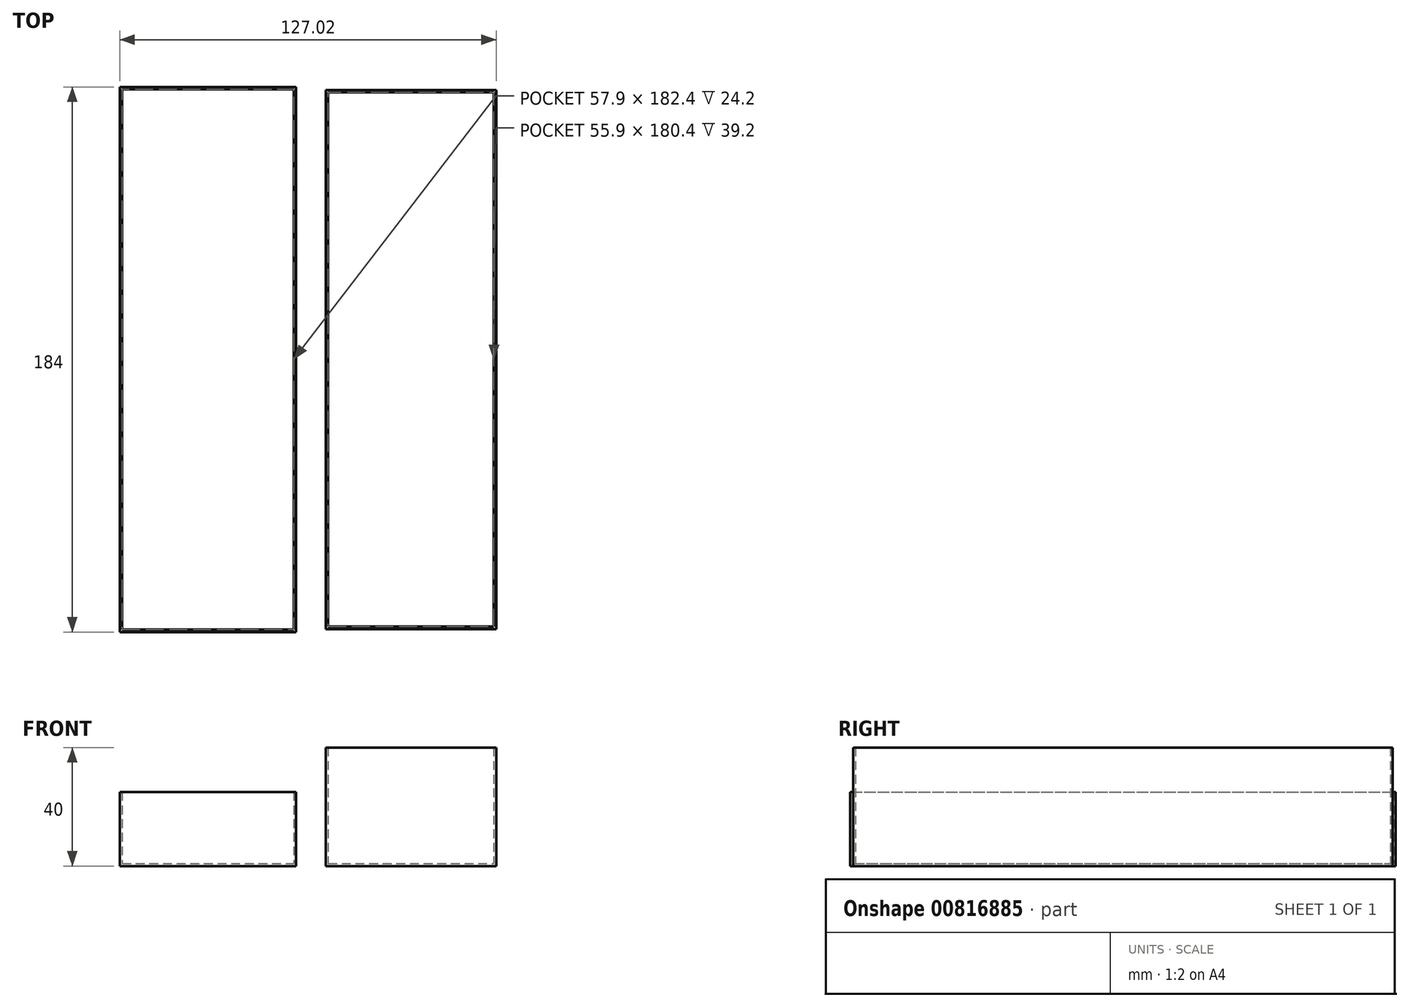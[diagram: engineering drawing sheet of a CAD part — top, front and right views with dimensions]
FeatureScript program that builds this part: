
annotation { "Feature Type Name" : "Feature", "Feature Type Description" : "" }
export const myFeature = defineFeature(function(context is Context, id is Id, definition is map)
    precondition{}
    {
        {
            var Q0;
            Q0=qCreatedBy(makeId("Top.planeOp"),FACE);
            var sketch = newSketch(context, id + "F0", { "sketchPlane" : qUnion([Q0])});
            skLineSegment(sketch, "E0.bottom", {"start": v(91, -28.75) * mm, "end": v(-91, -28.75) * mm});
            skLineSegment(sketch, "E0.top", {"start": v(91, 28.75) * mm, "end": v(-91, 28.75) * mm});
            skLineSegment(sketch, "E0.left", {"start": v(91, -28.75) * mm, "end": v(91, 28.75) * mm});
            skLineSegment(sketch, "E0.right", {"start": v(-91, -28.75) * mm, "end": v(-91, 28.75) * mm});
            skPoint(sketch, "E0.middle", {"position": v(0, 0) * mm});
            skSolve(sketch);
        }
        {
            var Q0;
            Q0=makeQuery(id+"F0.imprint","IMPRINT",FACE,{"disambiguationData":[TD([[makeQuery(id+"F0.imprint","IMPRINT",EDGE,{"derivedFrom":sQuery(id+"F0.wireOp",EDGE,"E0.bottom")}),-1.0]])]});
            extrude(context, id + "F1", {"entities" : qUnion([Q0]), "depth" : 40 * mm, "offsetDistance" : 25 * mm});
        }
        {
            var Q0;
            Q0=makeQuery(id+"F1.opExtrude","CAP_FACE",FACE,{"disambiguationData":[OSD([sQuery(id+"F0.wireOp",EDGE,"E0.bottom"),sQuery(id+"F0.wireOp",EDGE,"E0.top"),sQuery(id+"F0.wireOp",EDGE,"E0.left"),sQuery(id+"F0.wireOp",EDGE,"E0.right")])],"isStart":false});
            shell(context, id + "F2", {"entities" : qUnion([Q0]), "thickness" : 0.8 * mm});
        }
        {
            var Q0;
            Q0=qCreatedBy(makeId("Top.planeOp"),FACE);
            var sketch = newSketch(context, id + "F3", { "sketchPlane" : qUnion([Q0])});
            skLineSegment(sketch, "E1.bottom", {"start": v(92, -98.27) * mm, "end": v(-92, -98.27) * mm});
            skLineSegment(sketch, "E1.top", {"start": v(92, -38.77) * mm, "end": v(-92, -38.77) * mm});
            skLineSegment(sketch, "E1.left", {"start": v(92, -98.27) * mm, "end": v(92, -38.77) * mm});
            skLineSegment(sketch, "E1.right", {"start": v(-92, -98.27) * mm, "end": v(-92, -38.77) * mm});
            skPoint(sketch, "E1.middle", {"position": v(0, -68.52) * mm});
            skSolve(sketch);
        }
        {
            var Q0;
            Q0=makeQuery(id+"F3.imprint","IMPRINT",FACE,{"disambiguationData":[TD([[makeQuery(id+"F3.imprint","IMPRINT",EDGE,{"derivedFrom":sQuery(id+"F3.wireOp",EDGE,"E1.bottom")}),-1.0]])]});
            extrude(context, id + "F4", {"entities" : qUnion([Q0]), "depth" : 25 * mm, "offsetDistance" : 25 * mm});
        }
        {
            var Q0;
            Q0=makeQuery(id+"F4.opExtrude","CAP_FACE",FACE,{"disambiguationData":[OSD([sQuery(id+"F3.wireOp",EDGE,"E1.bottom"),sQuery(id+"F3.wireOp",EDGE,"E1.top"),sQuery(id+"F3.wireOp",EDGE,"E1.left"),sQuery(id+"F3.wireOp",EDGE,"E1.right")])],"isStart":false});
            shell(context, id + "F5", {"entities" : qUnion([Q0]), "thickness" : 0.8 * mm});
        }
        {
            var Q0;
            Q0=makeQuery(id+"F1.opExtrude","SWEPT_BODY",BODY,{"disambiguationData":[OSD([sQuery(id+"F0.wireOp",EDGE,"E0.bottom"),sQuery(id+"F0.wireOp",EDGE,"E0.top"),sQuery(id+"F0.wireOp",EDGE,"E0.left"),sQuery(id+"F0.wireOp",EDGE,"E0.right")])]});
            var Q1;
            Q1=makeQuery(id+"F4.opExtrude","SWEPT_BODY",BODY,{"disambiguationData":[OSD([sQuery(id+"F3.wireOp",EDGE,"E1.bottom"),sQuery(id+"F3.wireOp",EDGE,"E1.top"),sQuery(id+"F3.wireOp",EDGE,"E1.left"),sQuery(id+"F3.wireOp",EDGE,"E1.right")])]});
            var Q2;
            Q2=makeQuery(id+"F1.opExtrude","SWEPT_EDGE",EDGE,{"disambiguationData":[OSD([sQuery(id+"F0.wireOp",EDGE,"E0.bottom"),sQuery(id+"F0.wireOp",EDGE,"E0.right")])]});
            transform(context, id + "F6", {"entities" : qUnion([Q0, Q1]), "transformType" : TransformType.ROTATION, "transformAxis" : qUnion([Q2]), "angle" : 90 * degree, "makeCopy" : false});
        }
    });
